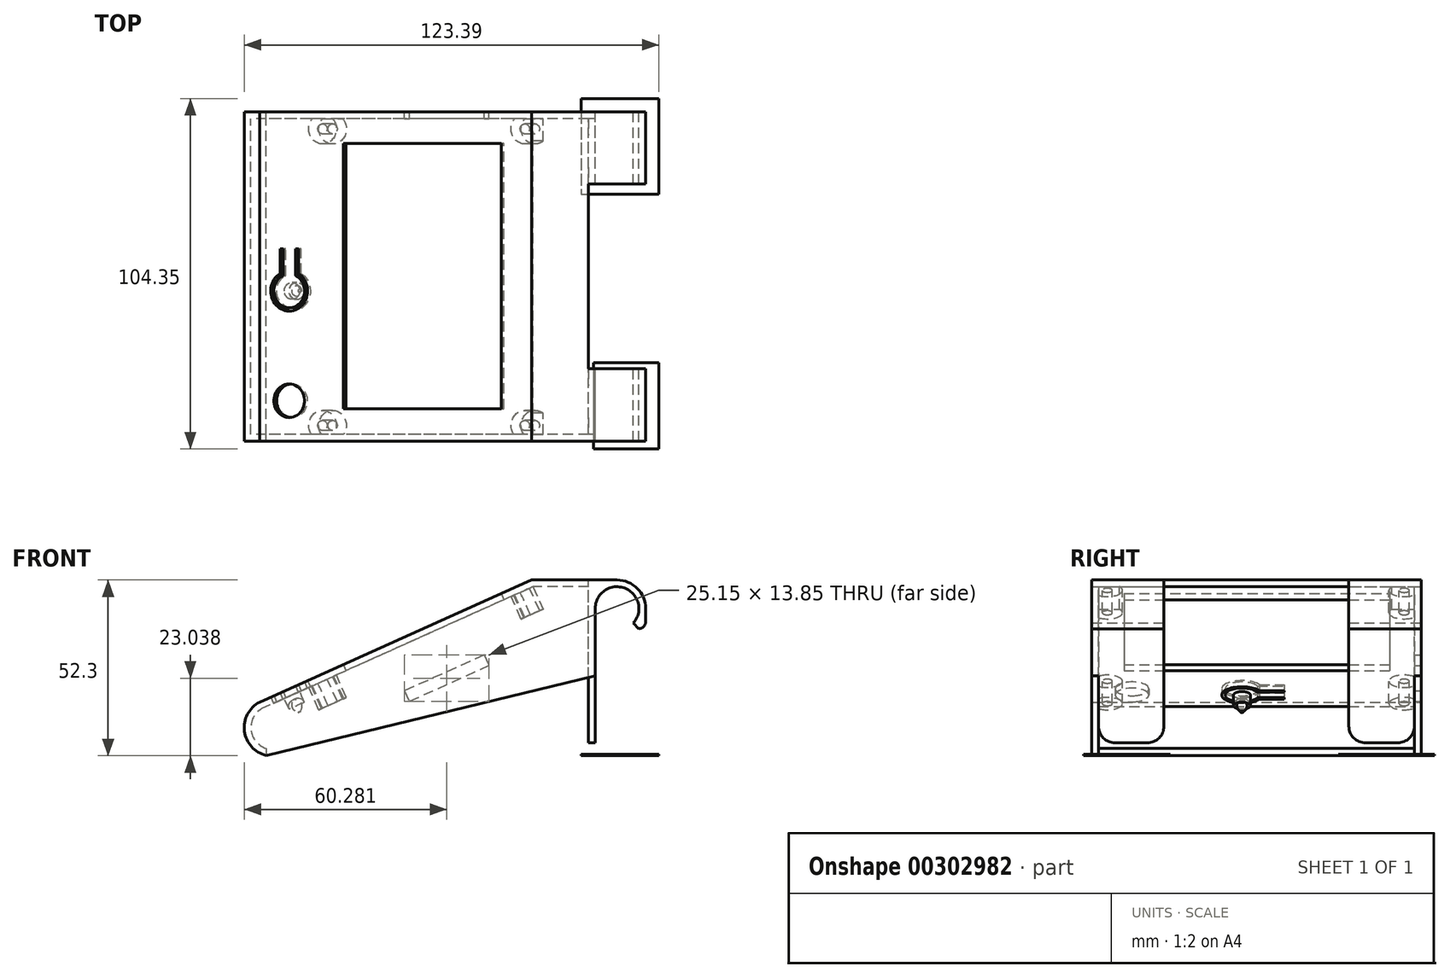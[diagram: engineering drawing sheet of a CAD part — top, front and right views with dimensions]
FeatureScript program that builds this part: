
annotation { "Feature Type Name" : "Feature", "Feature Type Description" : "" }
export const myFeature = defineFeature(function(context is Context, id is Id, definition is map)
    precondition{}
    {
        {
            var Q0;
            Q0=qCreatedBy(makeId("Front.planeOp"),FACE);
            var sketch = newSketch(context, id + "F0", { "sketchPlane" : qUnion([Q0])});
            skLineSegment(sketch, "E0", {"start": v(0, 0) * mm, "end": v(0, -42.85) * mm, "construction": true});
            skLineSegment(sketch, "E1", {"start": v(0, -42.85) * mm, "end": v(-104.35, -42.85) * mm, "construction": true});
            skLineSegment(sketch, "E2", {"start": v(-8.5, 6.5) * mm, "end": v(-25, 6.5) * mm});
            skLineSegment(sketch, "E3", {"start": v(-25, 6.5) * mm, "end": v(-104.35, -29.17) * mm});
            skLineSegment(sketch, "E4", {"start": v(-104.35, -29.17) * mm, "end": v(-104.35, -29.2) * mm});
            skLineSegment(sketch, "E5", {"start": v(-104.35, -29.17) * mm, "end": v(-98.2, -42.85) * mm, "construction": true});
            skLineSegment(sketch, "E6", {"start": v(-25, 6.5) * mm, "end": v(-18.85, -7.18) * mm, "construction": true});
            skLineSegment(sketch, "E7", {"start": v(-6.5, 0) * mm, "end": v(-6.5, -20) * mm});
            skArc(sketch, "E8.0", {"start": v(8.5, 0) * mm, "mid": v(6.01, 6.01) * mm, "end": v(0, 8.5) * mm});
            skLineSegment(sketch, "E9.1", {"start": v(-25.43, 8.5) * mm, "end": v(-106.35, -27.87) * mm});
            skLineSegment(sketch, "E9.2", {"start": v(0, 8.5) * mm, "end": v(-25.43, 8.5) * mm});
            skLineSegment(sketch, "E10", {"start": v(8.5, 0) * mm, "end": v(8.5, -6) * mm});
            skLineSegment(sketch, "E11", {"start": v(8.5, -6) * mm, "end": v(6.5, -6) * mm});
            skLineSegment(sketch, "E12", {"start": v(-8.5, 0) * mm, "end": v(-8.5, -20) * mm});
            skLineSegment(sketch, "E13", {"start": v(-8.5, -20) * mm, "end": v(-6.5, -20) * mm});
            skLineSegment(sketch, "E14", {"start": v(-8.5, 0) * mm, "end": v(-8.5, 6.5) * mm});
            skPoint(sketch, "E15.orphan", {"position": v(0, 6.5) * mm});
            skArc(sketch, "E16", {"start": v(-105.43, -27.46) * mm, "mid": v(-110.9, -36) * mm, "end": v(-104.35, -43.73) * mm});
            skPoint(sketch, "E16.third.point", {"position": v(-95.6, -40.58) * mm});
            skArc(sketch, "E17.0", {"start": v(-104.34, -29.2) * mm, "mid": v(-108.93, -35.42) * mm, "end": v(-104.35, -41.66) * mm});
            skLineSegment(sketch, "E18.trimOffspring", {"start": v(-104.35, -41.66) * mm, "end": v(-104.35, -42.85) * mm});
            skLineSegment(sketch, "E19", {"start": v(-104.35, -42.85) * mm, "end": v(-104.35, -43.73) * mm});
            skArc(sketch, "E20", {"start": v(4.85, -4.33) * mm, "mid": v(2.32, 6.07) * mm, "end": v(-6.5, 0) * mm});
            skLineSegment(sketch, "E21", {"start": v(6.5, -6) * mm, "end": v(4.85, -4.33) * mm});
            skSolve(sketch);
        }
        {
            var Q0;
            Q0=makeQuery(id+"F0.imprint","IMPRINT",FACE,{"disambiguationData":[TD([[makeQuery(id+"F0.imprint","IMPRINT",EDGE,{"derivedFrom":sQuery(id+"F0.wireOp",EDGE,"BKP1fskQ-plHT-HgYq-gCD3-4WAbrrdzwZiy")}),-1.0]])]});
            var Q1;
            Q1=makeQuery(id+"F0.imprint","IMPRINT",FACE,{"disambiguationData":[TD([[makeQuery(id+"F0.imprint","IMPRINT",EDGE,{"derivedFrom":sQuery(id+"F0.wireOp",EDGE,"E2")}),-1.0]])]});
            extrude(context, id + "F1", {"entities" : qUnion([Q0, Q1]), "endBound" : BoundingType.SYMMETRIC, "depth" : 98 * mm, "offsetDistance" : 25 * mm});
        }
        {
            var Q0;
            Q0=makeQuery(id+"F1.opExtrude","SWEPT_FACE",FACE,{"disambiguationData":[OSD([sQuery(id+"F0.wireOp",EDGE,"E3")])]});
            var sketch = newSketch(context, id + "F2", { "sketchPlane" : qUnion([Q0])});
            skLineSegment(sketch, "E22", {"start": v(-20.14, 44.35) * mm, "end": v(-22.79, 44.35) * mm, "construction": true});
            skCircle(sketch, "E23", {"center": v(-22.79, 44.35) * mm, "radius": 1.5 * mm});
            skCircle(sketch, "E24", {"center": v(-22.79, 44.35) * mm, "radius": 4.5 * mm});
            skLineSegment(sketch, "E25", {"start": v(-22.79, 44.35) * mm, "end": v(-22.79, -43.95) * mm, "construction": true});
            skCircle(sketch, "E26", {"center": v(-22.79, -43.95) * mm, "radius": 1.5 * mm});
            skCircle(sketch, "E27", {"center": v(-22.79, -43.95) * mm, "radius": 4.5 * mm});
            skLineSegment(sketch, "E28", {"start": v(-22.79, 44.35) * mm, "end": v(-88.79, 44.35) * mm, "construction": true});
            skCircle(sketch, "E29", {"center": v(-88.79, 44.35) * mm, "radius": 1.5 * mm});
            skCircle(sketch, "E30", {"center": v(-88.79, 44.35) * mm, "radius": 4.5 * mm});
            skLineSegment(sketch, "E31", {"start": v(-88.79, 44.35) * mm, "end": v(-88.79, -43.95) * mm, "construction": true});
            skCircle(sketch, "E32", {"center": v(-88.79, -43.95) * mm, "radius": 1.5 * mm});
            skCircle(sketch, "E33", {"center": v(-88.79, -43.95) * mm, "radius": 4.5 * mm});
            skLineSegment(sketch, "E34", {"start": v(-20.14, 39.4) * mm, "end": v(-29.64, 39.4) * mm, "construction": true});
            skLineSegment(sketch, "E35.bottom", {"start": v(-29.64, 39.4) * mm, "end": v(-81.14, 39.4) * mm});
            skLineSegment(sketch, "E35.top", {"start": v(-29.64, -39.6) * mm, "end": v(-81.14, -39.6) * mm});
            skLineSegment(sketch, "E35.left", {"start": v(-29.64, 39.4) * mm, "end": v(-29.64, -39.6) * mm});
            skLineSegment(sketch, "E35.right", {"start": v(-81.14, 39.4) * mm, "end": v(-81.14, -39.6) * mm});
            skLineSegment(sketch, "E36", {"start": v(-98.75, 49) * mm, "end": v(-98.75, 37) * mm, "construction": true});
            skCircle(sketch, "E37", {"center": v(-98.75, 37) * mm, "radius": 5 * mm});
            skLineSegment(sketch, "E38", {"start": v(-98.75, 37) * mm, "end": v(-98.75, 4.3) * mm, "construction": true});
            skArc(sketch, "E39", {"start": v(-96.75, -0.28) * mm, "mid": v(-98.75, 9.3) * mm, "end": v(-100.75, -0.28) * mm});
            skArc(sketch, "E40", {"start": v(-95.75, -0.9) * mm, "mid": v(-98.75, 10.3) * mm, "end": v(-101.75, -0.9) * mm});
            skLineSegment(sketch, "E41", {"start": v(-98.75, 9.82) * mm, "end": v(-98.75, 4.3) * mm, "construction": true});
            skLineSegment(sketch, "E42", {"start": v(-100.75, -0.28) * mm, "end": v(-100.75, -8.28) * mm});
            skLineSegment(sketch, "E43", {"start": v(-96.75, -0.28) * mm, "end": v(-96.75, -8.28) * mm});
            skLineSegment(sketch, "E44", {"start": v(-101.75, -0.9) * mm, "end": v(-101.75, -8.28) * mm});
            skLineSegment(sketch, "E45", {"start": v(-95.75, -0.9) * mm, "end": v(-95.75, -8.28) * mm});
            skLineSegment(sketch, "E46", {"start": v(-95.75, -8.28) * mm, "end": v(-96.75, -8.28) * mm});
            skLineSegment(sketch, "E47", {"start": v(-100.75, -8.28) * mm, "end": v(-101.75, -8.28) * mm});
            skSolve(sketch);
        }
        {
            var Q0;
            Q0=makeQuery(id+"F2.imprint","IMPRINT",FACE,{"disambiguationData":[TD([[makeQuery(id+"F2.imprint","IMPRINT",EDGE,{"derivedFrom":sQuery(id+"F2.wireOp",EDGE,"FYazuGxI-XyyZ-jJ84-9QZj-pF02LvgmxLtU")}),1.0]])]});
            var Q1;
            Q1=makeQuery(id+"F2.imprint","IMPRINT",FACE,{"disambiguationData":[TD([[makeQuery(id+"F2.imprint","IMPRINT",EDGE,{"derivedFrom":sQuery(id+"F2.wireOp",EDGE,"E35.bottom")}),1.0]])]});
            extrude(context, id + "F3", {"entities" : qUnion([Q0, Q1]), "operationType" : NewBodyOperationType.REMOVE, "oppositeDirection" : true, "depth" : 2 * mm, "offsetDistance" : 25 * mm});
        }
        {
            var Q0;
            Q0=makeQuery(id+"F2.imprint","IMPRINT",FACE,{"disambiguationData":[TD([[makeQuery(id+"F2.imprint","IMPRINT",EDGE,{"derivedFrom":sQuery(id+"F2.wireOp",EDGE,"E23")}),-1.0]])]});
            var Q1;
            Q1=makeQuery(id+"F2.imprint","IMPRINT",FACE,{"disambiguationData":[TD([[makeQuery(id+"F2.imprint","IMPRINT",EDGE,{"derivedFrom":sQuery(id+"F2.wireOp",EDGE,"E26")}),-1.0]])]});
            var Q2;
            Q2=makeQuery(id+"F2.imprint","IMPRINT",FACE,{"disambiguationData":[TD([[makeQuery(id+"F2.imprint","IMPRINT",EDGE,{"derivedFrom":sQuery(id+"F2.wireOp",EDGE,"E32")}),-1.0]])]});
            var Q3;
            Q3=makeQuery(id+"F2.imprint","IMPRINT",FACE,{"disambiguationData":[TD([[makeQuery(id+"F2.imprint","IMPRINT",EDGE,{"derivedFrom":sQuery(id+"F2.wireOp",EDGE,"E29")}),-1.0]])]});
            extrude(context, id + "F4", {"entities" : qUnion([Q0, Q1, Q2, Q3]), "operationType" : NewBodyOperationType.ADD, "depth" : 7.3 * mm, "offsetDistance" : 25 * mm});
        }
        {
            var Q0;
            Q0=makeQuery(id+"F1.opExtrude","CAP_FACE",FACE,{"disambiguationData":[OSD([sQuery(id+"F0.wireOp",EDGE,"BKP1fskQ-plHT-HgYq-gCD3-4WAbrrdzwZiy"),sQuery(id+"F0.wireOp",EDGE,"E2"),sQuery(id+"F0.wireOp",EDGE,"E3"),sQuery(id+"F0.wireOp",EDGE,"E4"),sQuery(id+"F0.wireOp",EDGE,"KLzS8VjV-iBDu-Stew-j29a-tq2aAh7S9TWP"),sQuery(id+"F0.wireOp",EDGE,"E7"),sQuery(id+"F0.wireOp",EDGE,"E8.0"),sQuery(id+"F0.wireOp",EDGE,"E9.1"),sQuery(id+"F0.wireOp",EDGE,"E9.2"),sQuery(id+"F0.wireOp",EDGE,"E10"),sQuery(id+"F0.wireOp",EDGE,"E11"),sQuery(id+"F0.wireOp",EDGE,"E12"),sQuery(id+"F0.wireOp",EDGE,"E13"),sQuery(id+"F0.wireOp",EDGE,"E14"),sQuery(id+"F0.wireOp",EDGE,"E16"),sQuery(id+"F0.wireOp",EDGE,"E17.0"),sQuery(id+"F0.wireOp",EDGE,"E18.trimOffspring"),sQuery(id+"F0.wireOp",EDGE,"E19")])],"isStart":false});
            var sketch = newSketch(context, id + "F5", { "sketchPlane" : qUnion([Q0])});
            skLineSegment(sketch, "E48", {"start": v(-6.5, -20) * mm, "end": v(-104.35, -43.73) * mm});
            skSolve(sketch);
        }
        {
            var Q0;
            Q0=makeQuery(id+"F5.imprint","IMPRINT",FACE,{"disambiguationData":[TD([[makeQuery(id+"F5.imprint","IMPRINT",EDGE,{"derivedFrom":sQuery(id+"F5.wireOp",EDGE,"E48")}),-1.0]])]});
            extrude(context, id + "F6", {"entities" : qUnion([Q0]), "operationType" : NewBodyOperationType.ADD, "oppositeDirection" : true, "depth" : 2 * mm, "offsetDistance" : 25 * mm});
        }
        {
            var Q0;
            Q0=makeQuery(id+"F1.opExtrude","CAP_FACE",FACE,{"disambiguationData":[OSD([sQuery(id+"F0.wireOp",EDGE,"BKP1fskQ-plHT-HgYq-gCD3-4WAbrrdzwZiy"),sQuery(id+"F0.wireOp",EDGE,"E2"),sQuery(id+"F0.wireOp",EDGE,"E3"),sQuery(id+"F0.wireOp",EDGE,"E4"),sQuery(id+"F0.wireOp",EDGE,"KLzS8VjV-iBDu-Stew-j29a-tq2aAh7S9TWP"),sQuery(id+"F0.wireOp",EDGE,"E7"),sQuery(id+"F0.wireOp",EDGE,"E8.0"),sQuery(id+"F0.wireOp",EDGE,"E9.1"),sQuery(id+"F0.wireOp",EDGE,"E9.2"),sQuery(id+"F0.wireOp",EDGE,"E10"),sQuery(id+"F0.wireOp",EDGE,"E11"),sQuery(id+"F0.wireOp",EDGE,"E12"),sQuery(id+"F0.wireOp",EDGE,"E13"),sQuery(id+"F0.wireOp",EDGE,"E14"),sQuery(id+"F0.wireOp",EDGE,"E16"),sQuery(id+"F0.wireOp",EDGE,"E17.0"),sQuery(id+"F0.wireOp",EDGE,"E18.trimOffspring"),sQuery(id+"F0.wireOp",EDGE,"E19")])],"isStart":true});
            var sketch = newSketch(context, id + "F7", { "sketchPlane" : qUnion([Q0])});
            skLineSegment(sketch, "E49", {"start": v(6.5, -20) * mm, "end": v(104.35, -43.73) * mm});
            skSolve(sketch);
        }
        {
            var Q0;
            Q0=makeQuery(id+"F7.imprint","IMPRINT",FACE,{"disambiguationData":[TD([[makeQuery(id+"F7.imprint","IMPRINT",EDGE,{"derivedFrom":sQuery(id+"F7.wireOp",EDGE,"E49")}),1.0]])]});
            extrude(context, id + "F8", {"entities" : qUnion([Q0]), "operationType" : NewBodyOperationType.ADD, "oppositeDirection" : true, "depth" : 2 * mm, "offsetDistance" : 25 * mm});
        }
        {
            var Q0;
            Q0=makeQuery(id+"F2.imprint","IMPRINT",FACE,{"disambiguationData":[TD([[makeQuery(id+"F2.imprint","IMPRINT",EDGE,{"derivedFrom":sQuery(id+"F2.wireOp",EDGE,"E37")}),1.0]])]});
            extrude(context, id + "F9", {"entities" : qUnion([Q0]), "operationType" : NewBodyOperationType.REMOVE, "oppositeDirection" : true, "depth" : 2 * mm, "offsetDistance" : 25 * mm});
        }
        {
            var Q0;
            {var subQ0=sQuery(id+"F0.wireOp",EDGE,"E19");var subQ1=sQuery(id+"F0.wireOp",EDGE,"E18.trimOffspring");var subQ2=sQuery(id+"F0.wireOp",EDGE,"E17.0");var subQ3=sQuery(id+"F0.wireOp",EDGE,"E14");var subQ4=sQuery(id+"F0.wireOp",EDGE,"E13");var subQ5=sQuery(id+"F0.wireOp",EDGE,"E12");var subQ6=sQuery(id+"F0.wireOp",EDGE,"E4");var subQ7=sQuery(id+"F0.wireOp",EDGE,"E3");var subQ8=sQuery(id+"F0.wireOp",EDGE,"E2");Q0=makeQuery(id+"F8.boolean.opBoolean","MERGE",FACE,{"derivedFrom":[makeQuery(id+"F1.opExtrude","CAP_FACE",FACE,{"disambiguationData":[OSD([sQuery(id+"F0.wireOp",EDGE,"BKP1fskQ-plHT-HgYq-gCD3-4WAbrrdzwZiy"),subQ8,subQ7,subQ6,sQuery(id+"F0.wireOp",EDGE,"KLzS8VjV-iBDu-Stew-j29a-tq2aAh7S9TWP"),sQuery(id+"F0.wireOp",EDGE,"E7"),sQuery(id+"F0.wireOp",EDGE,"E8.0"),sQuery(id+"F0.wireOp",EDGE,"E9.1"),sQuery(id+"F0.wireOp",EDGE,"E9.2"),sQuery(id+"F0.wireOp",EDGE,"E10"),sQuery(id+"F0.wireOp",EDGE,"E11"),subQ5,subQ4,subQ3,sQuery(id+"F0.wireOp",EDGE,"E16"),subQ2,subQ1,subQ0])],"isStart":true}),makeQuery(id+"F8.opExtrude","CAP_FACE",FACE,{"disambiguationData":[OSD([subQ8,subQ7,subQ6,subQ5,subQ4,subQ3,subQ2,subQ1,subQ0,sQuery(id+"F7.wireOp",EDGE,"E49")])],"isStart":true})]});}
            var sketch = newSketch(context, id + "F10", { "sketchPlane" : qUnion([Q0])});
            skLineSegment(sketch, "E50", {"start": v(25.43, 8.5) * mm, "end": v(19.44, -4.82) * mm, "construction": true});
            skLineSegment(sketch, "E51", {"start": v(19.44, -4.82) * mm, "end": v(39.5, -13.84) * mm, "construction": true});
            skLineSegment(sketch, "E52", {"start": v(39.5, -13.84) * mm, "end": v(63.22, -24.5) * mm});
            skLineSegment(sketch, "E53.0", {"start": v(38.07, -17.03) * mm, "end": v(61.79, -27.69) * mm});
            skLineSegment(sketch, "E54", {"start": v(39.5, -13.84) * mm, "end": v(38.07, -17.03) * mm});
            skLineSegment(sketch, "E55", {"start": v(63.22, -24.5) * mm, "end": v(61.79, -27.69) * mm});
            skSolve(sketch);
        }
        {
            var Q0;
            Q0=makeQuery(id+"F10.imprint","IMPRINT",FACE,{"disambiguationData":[TD([[makeQuery(id+"F10.imprint","IMPRINT",EDGE,{"derivedFrom":sQuery(id+"F10.wireOp",EDGE,"E52")}),-1.0]])]});
            extrude(context, id + "F11", {"entities" : qUnion([Q0]), "operationType" : NewBodyOperationType.REMOVE, "oppositeDirection" : true, "depth" : 2 * mm, "offsetDistance" : 25 * mm});
        }
        {
            var Q0;
            Q0=makeQuery(id+"F1.opExtrude","SWEPT_FACE",FACE,{"disambiguationData":[OSD([sQuery(id+"F0.wireOp",EDGE,"E9.2")])]});
            var sketch = newSketch(context, id + "F12", { "sketchPlane" : qUnion([Q0])});
            skLineSegment(sketch, "E56.bottom", {"start": v(8.5, 27.5) * mm, "end": v(-8.5, 27.5) * mm});
            skLineSegment(sketch, "E56.top", {"start": v(8.5, -27.5) * mm, "end": v(-8.5, -27.5) * mm});
            skLineSegment(sketch, "E56.left", {"start": v(8.5, 27.5) * mm, "end": v(8.5, -27.5) * mm});
            skLineSegment(sketch, "E56.right", {"start": v(-8.5, 27.5) * mm, "end": v(-8.5, -27.5) * mm});
            skPoint(sketch, "E56.middle", {"position": v(0, 0) * mm});
            skSolve(sketch);
        }
        {
            var Q0;
            {var subQ0=sQuery(id+"F12.wireOp",EDGE,"E56.left");Q0=makeQuery(id+"F12.imprint","IMPRINT",FACE,{"disambiguationData":[TD([[makeQuery(id+"F12.imprint","IMPRINT",EDGE,{"derivedFrom":subQ0}),-1.0]])]});}
            var Q1;
            {var subQ0=sQuery(id+"F12.wireOp",EDGE,"E56.right");Q1=makeQuery(id+"F12.imprint","IMPRINT",FACE,{"disambiguationData":[TD([[makeQuery(id+"F12.imprint","IMPRINT",EDGE,{"derivedFrom":subQ0}),1.0]])]});}
            extrude(context, id + "F13", {"entities" : qUnion([Q0, Q1]), "operationType" : NewBodyOperationType.REMOVE, "oppositeDirection" : true, "depth" : 40 * mm, "offsetDistance" : 25 * mm});
        }
        {
            var Q0;
            {var subQ0=sQuery(id+"F0.wireOp",EDGE,"E11");var subQ10=sQuery(id+"F0.wireOp",EDGE,"E10");Q0=makeQuery(id+"F13.boolean.opBoolean","SPLIT",EDGE,{"disambiguationData":[TD([makeQuery(id+"F13.opExtrude","SWEPT_FACE",FACE,{"disambiguationData":[OSD([sQuery(id+"F12.wireOp",EDGE,"E56.bottom")])]})])],"derivedFrom":makeQuery(id+"F1.opExtrude","SWEPT_EDGE",EDGE,{"disambiguationData":[OSD([subQ10,subQ0])]})});}
            var Q1;
            {var subQ9=sQuery(id+"F0.wireOp",EDGE,"E11");var subQ10=sQuery(id+"F0.wireOp",EDGE,"E10");Q1=makeQuery(id+"F13.boolean.opBoolean","SPLIT",EDGE,{"disambiguationData":[TD([makeQuery(id+"F13.opExtrude","SWEPT_FACE",FACE,{"disambiguationData":[OSD([sQuery(id+"F12.wireOp",EDGE,"E56.top")])]})])],"derivedFrom":makeQuery(id+"F1.opExtrude","SWEPT_EDGE",EDGE,{"disambiguationData":[OSD([subQ10,subQ9])]})});}
            fillet(context, id + "F14", {"entities" : qUnion([Q0, Q1]), "radius" : 2 * mm, "tangentPropagation" : true, "allowEdgeOverflow" : false});
        }
        {
            var Q0;
            {var subQ0=sQuery(id+"F5.wireOp",EDGE,"E48");var subQ2=sQuery(id+"F0.wireOp",EDGE,"E13");Q0=makeQuery(id+"F13.boolean.opBoolean","SPLIT",FACE,{"disambiguationData":[TD([makeQuery(id+"F6.opExtrude","SWEPT_FACE",FACE,{"disambiguationData":[OSD([subQ0])]})])],"derivedFrom":makeQuery(id+"F1.opExtrude","SWEPT_FACE",FACE,{"disambiguationData":[OSD([subQ2])]})});}
            var sketch = newSketch(context, id + "F15", { "sketchPlane" : qUnion([Q0])});
            skLineSegment(sketch, "E57.bottom", {"start": v(-6.5, 27.5) * mm, "end": v(-8.5, 27.5) * mm});
            skLineSegment(sketch, "E57.top", {"start": v(-6.5, 47) * mm, "end": v(-8.5, 47) * mm});
            skLineSegment(sketch, "E57.left", {"start": v(-6.5, 27.5) * mm, "end": v(-6.5, 47) * mm});
            skLineSegment(sketch, "E57.right", {"start": v(-8.5, 27.5) * mm, "end": v(-8.5, 47) * mm});
            skSolve(sketch);
        }
        {
            var Q0;
            Q0=makeQuery(id+"F15.imprint","IMPRINT",FACE,{"disambiguationData":[TD([[makeQuery(id+"F15.imprint","IMPRINT",EDGE,{"derivedFrom":sQuery(id+"F15.wireOp",EDGE,"E57.bottom")}),-1.0]])]});
            extrude(context, id + "F16", {"entities" : qUnion([Q0]), "operationType" : NewBodyOperationType.ADD, "depth" : 20 * mm, "offsetDistance" : 25 * mm});
        }
        {
            var Q0;
            {var subQ0=sQuery(id+"F7.wireOp",EDGE,"E49");var subQ3=sQuery(id+"F0.wireOp",EDGE,"E13");Q0=makeQuery(id+"F13.boolean.opBoolean","SPLIT",FACE,{"disambiguationData":[TD([makeQuery(id+"F8.opExtrude","SWEPT_FACE",FACE,{"disambiguationData":[OSD([subQ0])]})])],"derivedFrom":makeQuery(id+"F1.opExtrude","SWEPT_FACE",FACE,{"disambiguationData":[OSD([subQ3])]})});}
            var sketch = newSketch(context, id + "F17", { "sketchPlane" : qUnion([Q0])});
            skLineSegment(sketch, "E58.bottom", {"start": v(-6.5, -27.5) * mm, "end": v(-8.5, -27.5) * mm});
            skLineSegment(sketch, "E58.top", {"start": v(-6.5, -47) * mm, "end": v(-8.5, -47) * mm});
            skLineSegment(sketch, "E58.left", {"start": v(-6.5, -27.5) * mm, "end": v(-6.5, -47) * mm});
            skLineSegment(sketch, "E58.right", {"start": v(-8.5, -27.5) * mm, "end": v(-8.5, -47) * mm});
            skSolve(sketch);
        }
        {
            var Q0;
            Q0=makeQuery(id+"F17.imprint","IMPRINT",FACE,{"disambiguationData":[TD([[makeQuery(id+"F17.imprint","IMPRINT",EDGE,{"derivedFrom":sQuery(id+"F17.wireOp",EDGE,"E58.bottom")}),1.0]])]});
            extrude(context, id + "F18", {"entities" : qUnion([Q0]), "operationType" : NewBodyOperationType.ADD, "depth" : 20 * mm, "offsetDistance" : 25 * mm});
        }
        {
            var Q0;
            Q0=makeQuery(id+"F18.opExtrude","CAP_EDGE",EDGE,{"disambiguationData":[OSD([sQuery(id+"F17.wireOp",EDGE,"E58.top")])],"isStart":false});
            var Q1;
            Q1=makeQuery(id+"F18.opExtrude","CAP_EDGE",EDGE,{"disambiguationData":[OSD([sQuery(id+"F17.wireOp",EDGE,"E58.bottom")])],"isStart":false});
            var Q2;
            Q2=makeQuery(id+"F16.opExtrude","CAP_EDGE",EDGE,{"disambiguationData":[OSD([sQuery(id+"F15.wireOp",EDGE,"E57.bottom")])],"isStart":false});
            var Q3;
            Q3=makeQuery(id+"F16.opExtrude","CAP_EDGE",EDGE,{"disambiguationData":[OSD([sQuery(id+"F15.wireOp",EDGE,"E57.top")])],"isStart":false});
            fillet(context, id + "F19", {"entities" : qUnion([Q0, Q1, Q2, Q3]), "radius" : 5 * mm, "tangentPropagation" : true, "allowEdgeOverflow" : false});
        }
        {
            var Q0;
            Q0=makeQuery(id+"F2.imprint","IMPRINT",FACE,{"disambiguationData":[TD([[makeQuery(id+"F2.imprint","IMPRINT",EDGE,{"derivedFrom":sQuery(id+"F2.wireOp",EDGE,"E39")}),-1.0]])]});
            extrude(context, id + "F20", {"entities" : qUnion([Q0]), "operationType" : NewBodyOperationType.REMOVE, "oppositeDirection" : true, "depth" : 2 * mm, "offsetDistance" : 25 * mm});
        }
        {
            var Q0;
            Q0=makeQuery(id+"F1.opExtrude","SWEPT_FACE",FACE,{"disambiguationData":[OSD([sQuery(id+"F0.wireOp",EDGE,"E9.1")])]});
            var sketch = newSketch(context, id + "F21", { "sketchPlane" : qUnion([Q0])});
            skCircle(sketch, "E59", {"center": v(-98.75, -4.3) * mm, "radius": 4.5 * mm});
            skCircle(sketch, "E60", {"center": v(-98.75, -4.3) * mm, "radius": 2.5 * mm});
            skSolve(sketch);
        }
        {
            var Q0;
            Q0=makeQuery(id+"F21.imprint","IMPRINT",FACE,{"disambiguationData":[TD([[makeQuery(id+"F21.imprint","IMPRINT",EDGE,{"derivedFrom":sQuery(id+"F21.wireOp",EDGE,"E60")}),1.0]])]});
            extrude(context, id + "F22", {"entities" : qUnion([Q0]), "operationType" : NewBodyOperationType.ADD, "oppositeDirection" : true, "depth" : 7.5 * mm, "offsetDistance" : 25 * mm});
        }
        {
            var Q0;
            Q0=makeQuery(id+"F22.opExtrude","CAP_EDGE",EDGE,{"disambiguationData":[OSD([sQuery(id+"F21.wireOp",EDGE,"E60")])],"isStart":false});
            fillet(context, id + "F23", {"entities" : qUnion([Q0]), "radius" : 2 * mm, "tangentPropagation" : true, "allowEdgeOverflow" : false});
        }
        {
            var Q0;
            Q0=makeQuery(id+"F1.opExtrude","SWEPT_BODY",BODY,{"disambiguationData":[OSD([sQuery(id+"F0.wireOp",EDGE,"E2"),sQuery(id+"F0.wireOp",EDGE,"E3"),sQuery(id+"F0.wireOp",EDGE,"E4"),sQuery(id+"F0.wireOp",EDGE,"E7"),sQuery(id+"F0.wireOp",EDGE,"E8.0"),sQuery(id+"F0.wireOp",EDGE,"E9.1"),sQuery(id+"F0.wireOp",EDGE,"E9.2"),sQuery(id+"F0.wireOp",EDGE,"E10"),sQuery(id+"F0.wireOp",EDGE,"E11"),sQuery(id+"F0.wireOp",EDGE,"E12"),sQuery(id+"F0.wireOp",EDGE,"E13"),sQuery(id+"F0.wireOp",EDGE,"E14"),sQuery(id+"F0.wireOp",EDGE,"E16"),sQuery(id+"F0.wireOp",EDGE,"E17.0"),sQuery(id+"F0.wireOp",EDGE,"E18.trimOffspring"),sQuery(id+"F0.wireOp",EDGE,"E19"),sQuery(id+"F0.wireOp",EDGE,"E20"),sQuery(id+"F0.wireOp",EDGE,"E21")])]});
            transform(context, id + "F24", {"entities" : qUnion([Q0]), "transformType" : TransformType.TRANSLATION_3D, "dx" : 53.5 * mm, "dy" : 0 * mm, "dz" : 43.8 * mm, "makeCopy" : false});
        }
        {
            var Q0;
            Q0=qCreatedBy(makeId("Top.planeOp"),FACE);
            var sketch = newSketch(context, id + "F25", { "sketchPlane" : qUnion([Q0])});
            skLineSegment(sketch, "E61.bottom", {"start": v(46.55, -25.67) * mm, "end": v(65.96, -25.67) * mm});
            skLineSegment(sketch, "E61.top", {"start": v(46.55, -51.36) * mm, "end": v(65.96, -51.36) * mm});
            skLineSegment(sketch, "E61.left", {"start": v(46.55, -25.67) * mm, "end": v(46.55, -51.36) * mm});
            skLineSegment(sketch, "E61.right", {"start": v(65.96, -25.67) * mm, "end": v(65.96, -51.36) * mm});
            skLineSegment(sketch, "E62.bottom", {"start": v(42.9, 53) * mm, "end": v(65.96, 53) * mm});
            skLineSegment(sketch, "E62.top", {"start": v(42.9, 24.45) * mm, "end": v(65.96, 24.45) * mm});
            skLineSegment(sketch, "E62.left", {"start": v(42.9, 53) * mm, "end": v(42.9, 24.45) * mm});
            skLineSegment(sketch, "E62.right", {"start": v(65.96, 53) * mm, "end": v(65.96, 24.45) * mm});
            skSolve(sketch);
        }
        {
            var Q0;
            Q0=makeQuery(id+"F25.imprint","IMPRINT",FACE,{"disambiguationData":[TD([[makeQuery(id+"F25.imprint","IMPRINT",EDGE,{"derivedFrom":sQuery(id+"F25.wireOp",EDGE,"E62.bottom")}),-1.0]])]});
            var Q1;
            Q1=makeQuery(id+"F25.imprint","IMPRINT",FACE,{"disambiguationData":[TD([[makeQuery(id+"F25.imprint","IMPRINT",EDGE,{"derivedFrom":sQuery(id+"F25.wireOp",EDGE,"E61.bottom")}),-1.0]])]});
            extrude(context, id + "F26", {"entities" : qUnion([Q0, Q1]), "depth" : 0.4 * mm, "offsetDistance" : 25 * mm});
        }
    });
